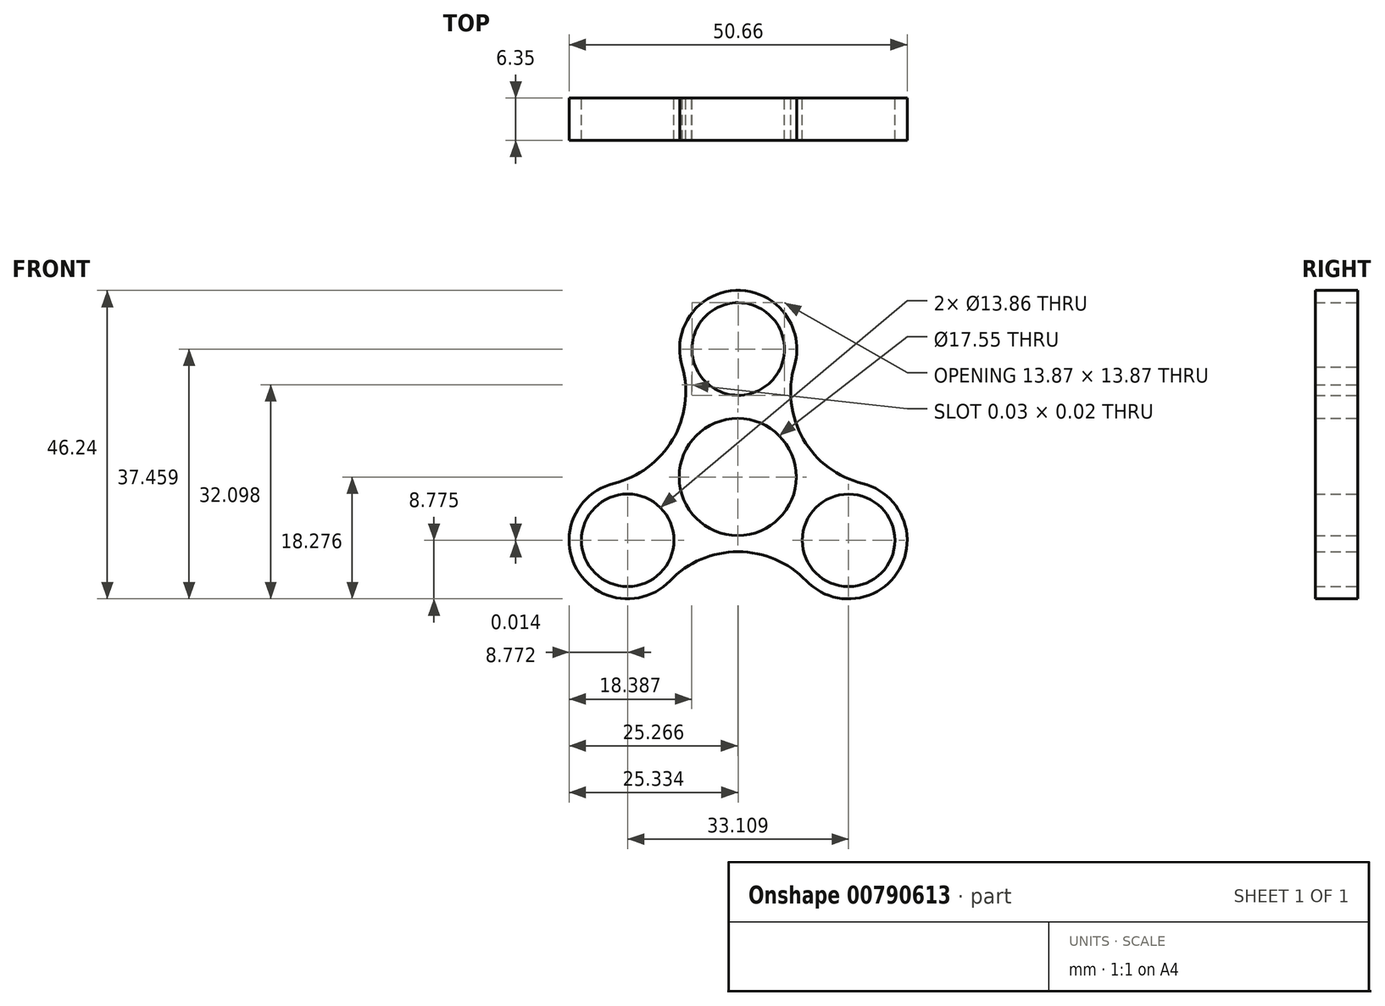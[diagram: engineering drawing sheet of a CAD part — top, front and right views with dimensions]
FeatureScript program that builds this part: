
annotation { "Feature Type Name" : "Feature", "Feature Type Description" : "" }
export const myFeature = defineFeature(function(context is Context, id is Id, definition is map)
    precondition{}
    {
        {
            var Q0;
            Q0=qCreatedBy(makeId("Front.planeOp"),FACE);
            var sketch = newSketch(context, id + "F0", { "sketchPlane" : qUnion([Q0])});
            skCircle(sketch, "E0", {"center": v(0, 0) * mm, "radius": 6.95 * mm});
            skCircle(sketch, "E1", {"center": v(0, 19.12) * mm, "radius": 6.93 * mm});
            skArc(sketch, "E2", {"start": v(8.78, 19.12) * mm, "mid": v(-1.36, 27.8) * mm, "end": v(-8.35, 16.43) * mm});
            skCircle(sketch, "E3", {"center": v(-0.06, -0.06) * mm, "radius": 8.78 * mm});
            skLineSegment(sketch, "E4", {"start": v(6.93, 18.94) * mm, "end": v(6.93, 18.73) * mm});
            skLineSegment(sketch, "E5", {"start": v(-6.95, 13.77) * mm, "end": v(-6.95, 13.77) * mm});
            skArc(sketch, "E6.1.0", {"start": v(8.43, 16.65) * mm, "mid": v(0.01, 27.9) * mm, "end": v(-8.42, 16.66) * mm});
            skLineSegment(sketch, "E6.1.2", {"start": v(-6.93, 13.74) * mm, "end": v(-6.93, 13.74) * mm});
            skArc(sketch, "E7.1.0", {"start": v(-18.64, -1.03) * mm, "mid": v(-24.16, -13.94) * mm, "end": v(-10.22, -15.62) * mm});
            skCircle(sketch, "E7.1.1", {"center": v(-16.56, -9.55) * mm, "radius": 6.93 * mm});
            skLineSegment(sketch, "E7.1.3", {"start": v(-19.87, -3.47) * mm, "end": v(-19.69, -3.36) * mm});
            skArc(sketch, "E7.2.0", {"start": v(10.2, -15.63) * mm, "mid": v(24.15, -13.96) * mm, "end": v(18.64, -1.04) * mm});
            skCircle(sketch, "E7.2.1", {"center": v(16.55, -9.56) * mm, "radius": 6.93 * mm});
            skLineSegment(sketch, "E7.2.3", {"start": v(12.94, -15.47) * mm, "end": v(12.76, -15.37) * mm});
            skLineSegment(sketch, "E8", {"start": v(6.93, 19.12) * mm, "end": v(6.94, 19.12) * mm});
            skArc(sketch, "E9", {"start": v(8.43, 16.65) * mm, "mid": v(9.76, 5.63) * mm, "end": v(18.64, -1.04) * mm});
            skLineSegment(sketch, "E10.trimOffspring", {"start": v(6.94, 4) * mm, "end": v(6.93, 4) * mm});
            skLineSegment(sketch, "E11.trimOffspring", {"start": v(6.93, 4) * mm, "end": v(6.93, 4) * mm});
            skLineSegment(sketch, "E12.trimOffspring", {"start": v(6.93, 13.74) * mm, "end": v(6.93, 13.72) * mm});
            skLineSegment(sketch, "E13.trimOffspring", {"start": v(6.93, 0.54) * mm, "end": v(6.93, 0) * mm});
            skLineSegment(sketch, "E14.trimOffspring", {"start": v(-3.93, 5.73) * mm, "end": v(-3.46, 6) * mm});
            skLineSegment(sketch, "E15.trimOffspring", {"start": v(-3, -6.27) * mm, "end": v(-3.46, -6) * mm});
            skLineSegment(sketch, "E16.trimOffspring", {"start": v(16.55, -0.79) * mm, "end": v(16.55, -0.35) * mm});
            skLineSegment(sketch, "E17.trimOffspring", {"start": v(8.78, 19.12) * mm, "end": v(8.78, 19.12) * mm});
            skArc(sketch, "E18.1.0", {"start": v(-18.64, -1.03) * mm, "mid": v(-9.75, 5.64) * mm, "end": v(-8.42, 16.66) * mm});
            skArc(sketch, "E18.2.0", {"start": v(10.2, -15.63) * mm, "mid": v(0, -11.26) * mm, "end": v(-10.22, -15.62) * mm});
            skArc(sketch, "E19.trimOffspring", {"start": v(-6.95, 13.77) * mm, "mid": v(-6.94, 13.76) * mm, "end": v(-6.93, 13.74) * mm});
            skSolve(sketch);
        }
        {
            var Q0;
            Q0 = qSketchRegion(id + "F0", true);
            extrude(context, id + "F1", {"entities" : qUnion([Q0]), "depth" : 6.35 * mm, "offsetDistance" : 25.4 * mm});
        }
    });
